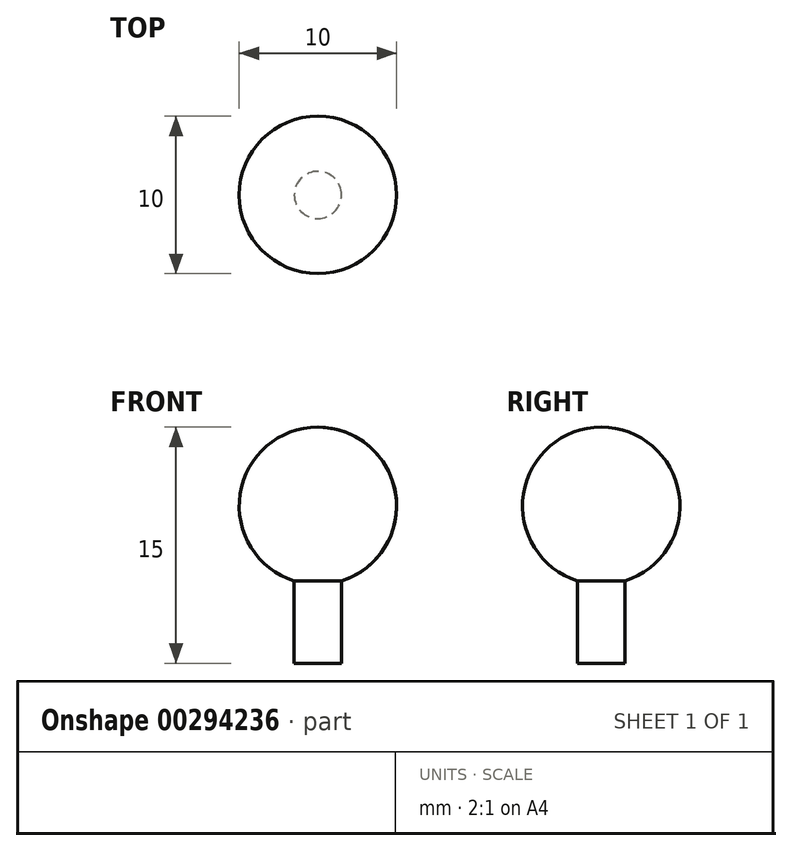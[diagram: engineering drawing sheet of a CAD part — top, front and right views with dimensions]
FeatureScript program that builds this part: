
annotation { "Feature Type Name" : "Feature", "Feature Type Description" : "" }
export const myFeature = defineFeature(function(context is Context, id is Id, definition is map)
    precondition{}
    {
        {
            var Q0;
            Q0=qCreatedBy(makeId("Front.planeOp"),FACE);
            var sketch = newSketch(context, id + "F0", { "sketchPlane" : qUnion([Q0])});
            skArc(sketch, "E0", {"start": v(1.5, -4.77) * mm, "mid": v(4.94, 0.76) * mm, "end": v(0, 5) * mm});
            skLineSegment(sketch, "E1.bottom", {"start": v(0, -10) * mm, "end": v(1.5, -10) * mm});
            skLineSegment(sketch, "E1.right", {"start": v(1.5, -10) * mm, "end": v(1.5, -4.77) * mm});
            skPoint(sketch, "E2.orphan", {"position": v(-1.5, 10) * mm});
            skPoint(sketch, "E3.orphan", {"position": v(1.5, 10) * mm});
            skLineSegment(sketch, "E4", {"start": v(0, 5) * mm, "end": v(0, -10) * mm});
            skPoint(sketch, "E5.orphan", {"position": v(-1.5, -10) * mm});
            skSolve(sketch);
        }
        {
            var Q0;
            Q0 = qSketchRegion(id + "F0", true);
            var Q1;
            Q1=sQuery(id+"F0.wireOp",EDGE,"E4");
            revolve(context, id + "F1", {"entities" : qUnion([Q0]), "axis" : qUnion([Q1]), "revolveType" : RevolveType.FULL});
        }
    });
